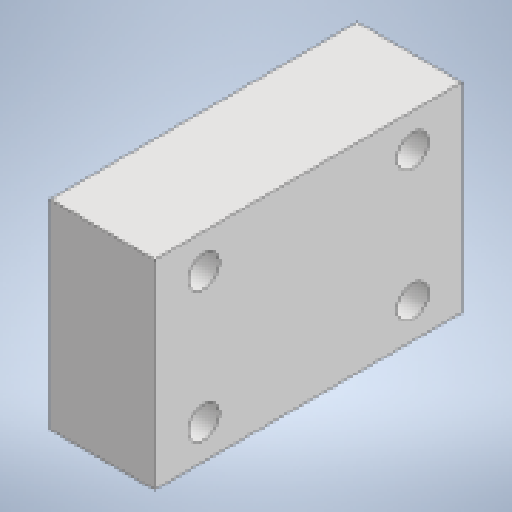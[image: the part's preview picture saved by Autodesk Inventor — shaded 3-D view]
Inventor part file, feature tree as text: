
AUTODESK INVENTOR PART (.ipt)
format: ipt  version: 2023 (Build 270158000, 158)  size: 148,480 bytes
history: native  units: mm
features: extrude x2, sketch x2
ambient origin geometry x8: Origin, YZ Plane, XZ Plane, XY Plane, X Axis, Y Axis, Z Axis, Center Point
bodies: Solid1 (feature_tree)
feature tree (4):
  extrude  "Extrusion1"  Depth=25.0mm
  extrude  "Extrusion2"  Depth=58.8mm
  sketch  "Sketch1"  dims[d0=6.0mm d1=25.0mm]
  sketch  "Sketch3"  dims[d2=40.0mm d3=58.8mm d4=38.2mm d5=20.0mm d6=0.0mm d7=150.0mm d8=2.0mm d9=30.0mm d12=60.0mm d13=16.0mm d14=20.0mm d15=0.0mm]
